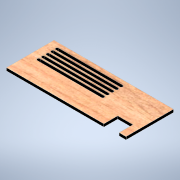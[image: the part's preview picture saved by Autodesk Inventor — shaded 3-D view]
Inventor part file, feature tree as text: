
AUTODESK INVENTOR PART (.ipt)
format: ipt  version: 2021 (Build 250183000, 183)  size: 155,136 bytes
history: native  units: mm
features: extrude x2, sketch x2, pattern_linear x1, projected_geometry x1
ambient origin geometry x8: Origin, YZ Plane, XZ Plane, XY Plane, X Axis, Y Axis, Z Axis, Center Point
bodies: Volumenkörper1 (feature_tree)
feature tree (6):
  extrude  "Extrusion1"  Depth=51.5mm
  extrude  "Extrusion2"  Depth=16.5mm
  pattern_linear  "Rechteckige Anordnung1"  Spacing1=7.5mm  [1 undecoded]
  sketch  "Skizze1"  dims[d0=129.5mm d1=51.5mm]
  sketch  "Skizze2"  dims[d2=3.0mm d3=0.0mm d4=16.5mm d5=7.5mm d6=15.0mm d7=5.0mm d8=10.0mm d9=50.0mm d10=1.5mm d11=0.0mm d12=0.0mm d13=50.0mm d15=5.0mm]
  projected_geometry  "Projizierte Kontur1"
note: 1 required parameter value undecoded (feature->parameter linkage not recoverable at this tier; creation-order binding heuristic only, values carry confidence <= 0.55)
